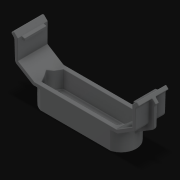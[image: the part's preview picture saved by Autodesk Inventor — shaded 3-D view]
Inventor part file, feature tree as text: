
AUTODESK INVENTOR PART (.ipt)
format: ipt  version: 2021 (Build 250183000, 183)  size: 726,016 bytes
history: native  units: in
note: dims shown in document units (in); Inventor stores cm internally (conversion verified against a paired STEP export)
features: fillet x1
ambient origin geometry x8: Origin, YZ Plane, XZ Plane, XY Plane, X Axis, Y Axis, Z Axis, Center Point
bodies: Solid1 (feature_tree)
feature tree (1):
  fillet  "Fillet6"  [1 undecoded]
note: 1 required parameter value undecoded (feature->parameter linkage not recoverable at this tier; creation-order binding heuristic only, values carry confidence <= 0.55)
